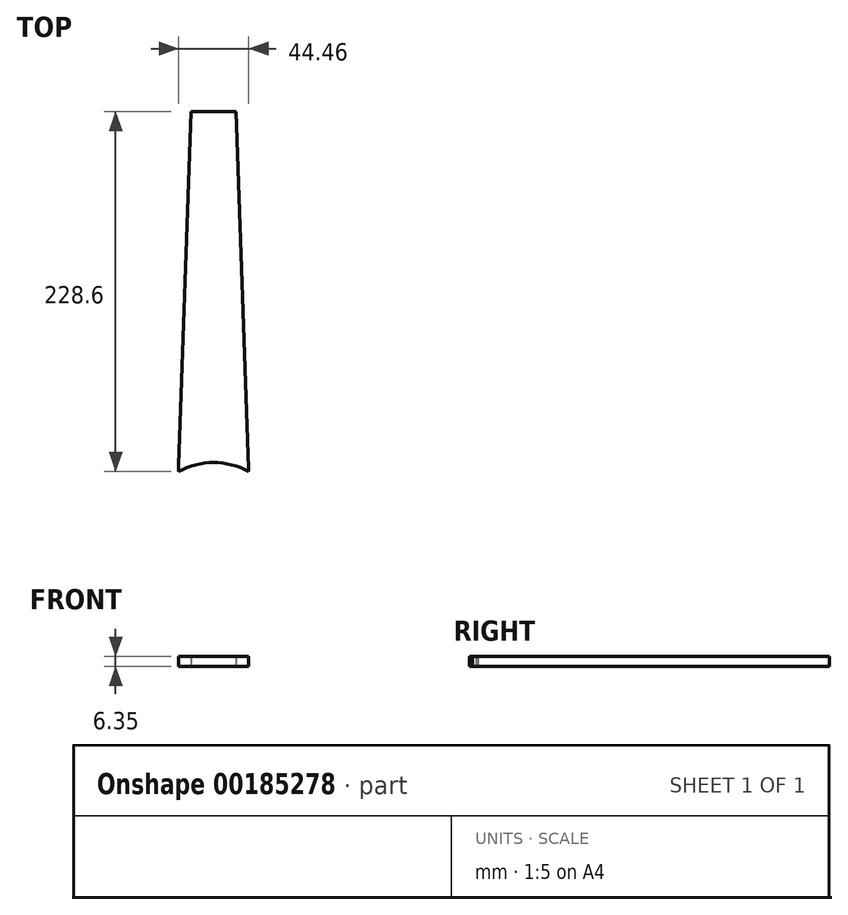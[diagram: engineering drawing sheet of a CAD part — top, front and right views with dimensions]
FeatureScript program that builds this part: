
annotation { "Feature Type Name" : "Feature", "Feature Type Description" : "" }
export const myFeature = defineFeature(function(context is Context, id is Id, definition is map)
    precondition{}
    {
        {
            var Q0;
            Q0=qCreatedBy(makeId("Top.planeOp"),FACE);
            var sketch = newSketch(context, id + "F0", { "sketchPlane" : qUnion([Q0])});
            skLineSegment(sketch, "E0.bottom", {"start": v(-22.22, 0) * mm, "end": v(22.22, 0) * mm});
            skLineSegment(sketch, "E0.top", {"start": v(-22.22, -228.6) * mm, "end": v(22.22, -228.6) * mm});
            skLineSegment(sketch, "E0.left", {"start": v(-22.22, 0) * mm, "end": v(-22.22, -228.6) * mm});
            skLineSegment(sketch, "E0.right", {"start": v(22.23, 0) * mm, "end": v(22.23, -228.6) * mm});
            skSolve(sketch);
        }
        {
            var Q0;
            Q0 = qSketchRegion(id + "F0", true);
            extrude(context, id + "F1", {"entities" : qUnion([Q0]), "oppositeDirection" : true, "depth" : 6.35 * mm});
        }
        {
            var Q0;
            Q0=makeQuery(id+"F1.opExtrude","SWEPT_FACE",FACE,{"disambiguationData":[OSD([sQuery(id+"F0.wireOp",EDGE,"E0.right")])]});
            var sketch = newSketch(context, id + "F2", { "sketchPlane" : qUnion([Q0])});
            skLineSegment(sketch, "E1.0", {"start": v(-21.03, -6.35) * mm, "end": v(-21.03, 0) * mm});
            skLineSegment(sketch, "E2.0", {"start": v(-40.87, -6.35) * mm, "end": v(-40.87, 0) * mm});
            skLineSegment(sketch, "E3.0", {"start": v(-59.61, -6.35) * mm, "end": v(-59.61, 0) * mm});
            skLineSegment(sketch, "E4.0", {"start": v(-77.3, -6.35) * mm, "end": v(-77.3, 0) * mm});
            skLineSegment(sketch, "E5.0", {"start": v(-93.98, -6.35) * mm, "end": v(-93.98, 0) * mm});
            skLineSegment(sketch, "E6.0", {"start": v(-109.73, -6.35) * mm, "end": v(-109.73, 0) * mm});
            skLineSegment(sketch, "E7.0", {"start": v(-124.61, -6.35) * mm, "end": v(-124.61, 0) * mm});
            skLineSegment(sketch, "E8.0", {"start": v(-138.63, -6.35) * mm, "end": v(-138.63, 0) * mm});
            skLineSegment(sketch, "E9.0", {"start": v(-151.9, -6.35) * mm, "end": v(-151.9, 0) * mm});
            skLineSegment(sketch, "E10.0", {"start": v(-164.39, -6.35) * mm, "end": v(-164.39, 0) * mm});
            skLineSegment(sketch, "E11.0", {"start": v(-176.17, -6.35) * mm, "end": v(-176.17, 0) * mm});
            skLineSegment(sketch, "E12.0", {"start": v(-187.33, -6.35) * mm, "end": v(-187.33, 0) * mm});
            skCircle(sketch, "E13", {"center": v(-21.03, 0) * mm, "radius": 0.8 * mm});
            skCircle(sketch, "E14", {"center": v(-40.87, 0) * mm, "radius": 0.8 * mm});
            skCircle(sketch, "E15", {"center": v(-59.61, 0) * mm, "radius": 0.8 * mm});
            skCircle(sketch, "E16", {"center": v(-77.3, 0) * mm, "radius": 0.8 * mm});
            skCircle(sketch, "E17", {"center": v(-93.98, 0) * mm, "radius": 0.8 * mm});
            skCircle(sketch, "E18", {"center": v(-109.73, 0) * mm, "radius": 0.8 * mm});
            skCircle(sketch, "E19", {"center": v(-124.61, 0) * mm, "radius": 0.8 * mm});
            skCircle(sketch, "E20", {"center": v(-138.63, 0) * mm, "radius": 0.8 * mm});
            skCircle(sketch, "E21", {"center": v(-151.9, 0) * mm, "radius": 0.8 * mm});
            skCircle(sketch, "E22", {"center": v(-164.39, 0) * mm, "radius": 0.8 * mm});
            skCircle(sketch, "E23", {"center": v(-176.17, 0) * mm, "radius": 0.8 * mm});
            skCircle(sketch, "E24", {"center": v(-187.33, 0) * mm, "radius": 0.8 * mm});
            skSolve(sketch);
        }
        {
            var Q0;
            {var subQ0=sQuery(id+"F2.wireOp",EDGE,"E1.0");var subQ1=makeQuery(id+"F1.opExtrude","CAP_EDGE",EDGE,{"disambiguationData":[OSD([sQuery(id+"F0.wireOp",EDGE,"E0.right")])],"isStart":true});var subQ2=makeQuery(id+"F2.imprint","INTERSECT",VERTEX,{"derivedFrom":[subQ1,subQ0]});Q0=makeQuery(id+"F2.imprint","IMPRINT",FACE,{"disambiguationData":[TD([[makeQuery(id+"F2.imprint","IMPRINT",EDGE,{"disambiguationData":[TD([[subQ2,1.0]])],"derivedFrom":subQ0}),1.0]])]});}
            var Q1;
            {var subQ0=sQuery(id+"F2.wireOp",EDGE,"E1.0");var subQ1=makeQuery(id+"F1.opExtrude","CAP_EDGE",EDGE,{"disambiguationData":[OSD([sQuery(id+"F0.wireOp",EDGE,"E0.right")])],"isStart":true});var subQ2=makeQuery(id+"F2.imprint","INTERSECT",VERTEX,{"derivedFrom":[subQ1,subQ0]});Q1=makeQuery(id+"F2.imprint","IMPRINT",FACE,{"disambiguationData":[TD([[makeQuery(id+"F2.imprint","IMPRINT",EDGE,{"disambiguationData":[TD([[subQ2,1.0]])],"derivedFrom":subQ0}),-1.0]])]});}
            var Q2;
            {var subQ0=sQuery(id+"F2.wireOp",EDGE,"E2.0");var subQ1=makeQuery(id+"F1.opExtrude","CAP_EDGE",EDGE,{"disambiguationData":[OSD([sQuery(id+"F0.wireOp",EDGE,"E0.right")])],"isStart":true});var subQ2=makeQuery(id+"F2.imprint","INTERSECT",VERTEX,{"derivedFrom":[subQ1,subQ0]});Q2=makeQuery(id+"F2.imprint","IMPRINT",FACE,{"disambiguationData":[TD([[makeQuery(id+"F2.imprint","IMPRINT",EDGE,{"disambiguationData":[TD([[subQ2,1.0]])],"derivedFrom":subQ0}),1.0]])]});}
            var Q3;
            {var subQ0=sQuery(id+"F2.wireOp",EDGE,"E2.0");var subQ1=makeQuery(id+"F1.opExtrude","CAP_EDGE",EDGE,{"disambiguationData":[OSD([sQuery(id+"F0.wireOp",EDGE,"E0.right")])],"isStart":true});var subQ2=makeQuery(id+"F2.imprint","INTERSECT",VERTEX,{"derivedFrom":[subQ1,subQ0]});Q3=makeQuery(id+"F2.imprint","IMPRINT",FACE,{"disambiguationData":[TD([[makeQuery(id+"F2.imprint","IMPRINT",EDGE,{"disambiguationData":[TD([[subQ2,1.0]])],"derivedFrom":subQ0}),-1.0]])]});}
            var Q4;
            {var subQ0=sQuery(id+"F2.wireOp",EDGE,"E3.0");var subQ1=makeQuery(id+"F1.opExtrude","CAP_EDGE",EDGE,{"disambiguationData":[OSD([sQuery(id+"F0.wireOp",EDGE,"E0.right")])],"isStart":true});var subQ2=makeQuery(id+"F2.imprint","INTERSECT",VERTEX,{"derivedFrom":[subQ1,subQ0]});Q4=makeQuery(id+"F2.imprint","IMPRINT",FACE,{"disambiguationData":[TD([[makeQuery(id+"F2.imprint","IMPRINT",EDGE,{"disambiguationData":[TD([[subQ2,1.0]])],"derivedFrom":subQ0}),1.0]])]});}
            var Q5;
            {var subQ0=sQuery(id+"F2.wireOp",EDGE,"E3.0");var subQ1=makeQuery(id+"F1.opExtrude","CAP_EDGE",EDGE,{"disambiguationData":[OSD([sQuery(id+"F0.wireOp",EDGE,"E0.right")])],"isStart":true});var subQ2=makeQuery(id+"F2.imprint","INTERSECT",VERTEX,{"derivedFrom":[subQ1,subQ0]});Q5=makeQuery(id+"F2.imprint","IMPRINT",FACE,{"disambiguationData":[TD([[makeQuery(id+"F2.imprint","IMPRINT",EDGE,{"disambiguationData":[TD([[subQ2,1.0]])],"derivedFrom":subQ0}),-1.0]])]});}
            var Q6;
            {var subQ0=sQuery(id+"F2.wireOp",EDGE,"E4.0");var subQ1=makeQuery(id+"F1.opExtrude","CAP_EDGE",EDGE,{"disambiguationData":[OSD([sQuery(id+"F0.wireOp",EDGE,"E0.right")])],"isStart":true});var subQ2=makeQuery(id+"F2.imprint","INTERSECT",VERTEX,{"derivedFrom":[subQ1,subQ0]});Q6=makeQuery(id+"F2.imprint","IMPRINT",FACE,{"disambiguationData":[TD([[makeQuery(id+"F2.imprint","IMPRINT",EDGE,{"disambiguationData":[TD([[subQ2,1.0]])],"derivedFrom":subQ0}),1.0]])]});}
            var Q7;
            {var subQ0=sQuery(id+"F2.wireOp",EDGE,"E4.0");var subQ1=makeQuery(id+"F1.opExtrude","CAP_EDGE",EDGE,{"disambiguationData":[OSD([sQuery(id+"F0.wireOp",EDGE,"E0.right")])],"isStart":true});var subQ2=makeQuery(id+"F2.imprint","INTERSECT",VERTEX,{"derivedFrom":[subQ1,subQ0]});Q7=makeQuery(id+"F2.imprint","IMPRINT",FACE,{"disambiguationData":[TD([[makeQuery(id+"F2.imprint","IMPRINT",EDGE,{"disambiguationData":[TD([[subQ2,1.0]])],"derivedFrom":subQ0}),-1.0]])]});}
            var Q8;
            {var subQ0=sQuery(id+"F2.wireOp",EDGE,"E5.0");var subQ1=makeQuery(id+"F1.opExtrude","CAP_EDGE",EDGE,{"disambiguationData":[OSD([sQuery(id+"F0.wireOp",EDGE,"E0.right")])],"isStart":true});var subQ2=makeQuery(id+"F2.imprint","INTERSECT",VERTEX,{"derivedFrom":[subQ1,subQ0]});Q8=makeQuery(id+"F2.imprint","IMPRINT",FACE,{"disambiguationData":[TD([[makeQuery(id+"F2.imprint","IMPRINT",EDGE,{"disambiguationData":[TD([[subQ2,1.0]])],"derivedFrom":subQ0}),1.0]])]});}
            var Q9;
            {var subQ0=sQuery(id+"F2.wireOp",EDGE,"E5.0");var subQ1=makeQuery(id+"F1.opExtrude","CAP_EDGE",EDGE,{"disambiguationData":[OSD([sQuery(id+"F0.wireOp",EDGE,"E0.right")])],"isStart":true});var subQ2=makeQuery(id+"F2.imprint","INTERSECT",VERTEX,{"derivedFrom":[subQ1,subQ0]});Q9=makeQuery(id+"F2.imprint","IMPRINT",FACE,{"disambiguationData":[TD([[makeQuery(id+"F2.imprint","IMPRINT",EDGE,{"disambiguationData":[TD([[subQ2,1.0]])],"derivedFrom":subQ0}),-1.0]])]});}
            var Q10;
            {var subQ0=sQuery(id+"F2.wireOp",EDGE,"E6.0");var subQ1=makeQuery(id+"F1.opExtrude","CAP_EDGE",EDGE,{"disambiguationData":[OSD([sQuery(id+"F0.wireOp",EDGE,"E0.right")])],"isStart":true});var subQ2=makeQuery(id+"F2.imprint","INTERSECT",VERTEX,{"derivedFrom":[subQ1,subQ0]});Q10=makeQuery(id+"F2.imprint","IMPRINT",FACE,{"disambiguationData":[TD([[makeQuery(id+"F2.imprint","IMPRINT",EDGE,{"disambiguationData":[TD([[subQ2,1.0]])],"derivedFrom":subQ0}),1.0]])]});}
            var Q11;
            {var subQ0=sQuery(id+"F2.wireOp",EDGE,"E6.0");var subQ1=makeQuery(id+"F1.opExtrude","CAP_EDGE",EDGE,{"disambiguationData":[OSD([sQuery(id+"F0.wireOp",EDGE,"E0.right")])],"isStart":true});var subQ2=makeQuery(id+"F2.imprint","INTERSECT",VERTEX,{"derivedFrom":[subQ1,subQ0]});Q11=makeQuery(id+"F2.imprint","IMPRINT",FACE,{"disambiguationData":[TD([[makeQuery(id+"F2.imprint","IMPRINT",EDGE,{"disambiguationData":[TD([[subQ2,1.0]])],"derivedFrom":subQ0}),-1.0]])]});}
            var Q12;
            {var subQ0=sQuery(id+"F2.wireOp",EDGE,"E7.0");var subQ1=makeQuery(id+"F1.opExtrude","CAP_EDGE",EDGE,{"disambiguationData":[OSD([sQuery(id+"F0.wireOp",EDGE,"E0.right")])],"isStart":true});var subQ2=makeQuery(id+"F2.imprint","INTERSECT",VERTEX,{"derivedFrom":[subQ1,subQ0]});Q12=makeQuery(id+"F2.imprint","IMPRINT",FACE,{"disambiguationData":[TD([[makeQuery(id+"F2.imprint","IMPRINT",EDGE,{"disambiguationData":[TD([[subQ2,1.0]])],"derivedFrom":subQ0}),1.0]])]});}
            var Q13;
            {var subQ0=sQuery(id+"F2.wireOp",EDGE,"E7.0");var subQ1=makeQuery(id+"F1.opExtrude","CAP_EDGE",EDGE,{"disambiguationData":[OSD([sQuery(id+"F0.wireOp",EDGE,"E0.right")])],"isStart":true});var subQ2=makeQuery(id+"F2.imprint","INTERSECT",VERTEX,{"derivedFrom":[subQ1,subQ0]});Q13=makeQuery(id+"F2.imprint","IMPRINT",FACE,{"disambiguationData":[TD([[makeQuery(id+"F2.imprint","IMPRINT",EDGE,{"disambiguationData":[TD([[subQ2,1.0]])],"derivedFrom":subQ0}),-1.0]])]});}
            var Q14;
            {var subQ0=sQuery(id+"F2.wireOp",EDGE,"E8.0");var subQ1=makeQuery(id+"F1.opExtrude","CAP_EDGE",EDGE,{"disambiguationData":[OSD([sQuery(id+"F0.wireOp",EDGE,"E0.right")])],"isStart":true});var subQ2=makeQuery(id+"F2.imprint","INTERSECT",VERTEX,{"derivedFrom":[subQ1,subQ0]});Q14=makeQuery(id+"F2.imprint","IMPRINT",FACE,{"disambiguationData":[TD([[makeQuery(id+"F2.imprint","IMPRINT",EDGE,{"disambiguationData":[TD([[subQ2,1.0]])],"derivedFrom":subQ0}),1.0]])]});}
            var Q15;
            {var subQ0=sQuery(id+"F2.wireOp",EDGE,"E8.0");var subQ1=makeQuery(id+"F1.opExtrude","CAP_EDGE",EDGE,{"disambiguationData":[OSD([sQuery(id+"F0.wireOp",EDGE,"E0.right")])],"isStart":true});var subQ2=makeQuery(id+"F2.imprint","INTERSECT",VERTEX,{"derivedFrom":[subQ1,subQ0]});Q15=makeQuery(id+"F2.imprint","IMPRINT",FACE,{"disambiguationData":[TD([[makeQuery(id+"F2.imprint","IMPRINT",EDGE,{"disambiguationData":[TD([[subQ2,1.0]])],"derivedFrom":subQ0}),-1.0]])]});}
            var Q16;
            {var subQ0=sQuery(id+"F2.wireOp",EDGE,"E9.0");var subQ1=makeQuery(id+"F1.opExtrude","CAP_EDGE",EDGE,{"disambiguationData":[OSD([sQuery(id+"F0.wireOp",EDGE,"E0.right")])],"isStart":true});var subQ2=makeQuery(id+"F2.imprint","INTERSECT",VERTEX,{"derivedFrom":[subQ1,subQ0]});Q16=makeQuery(id+"F2.imprint","IMPRINT",FACE,{"disambiguationData":[TD([[makeQuery(id+"F2.imprint","IMPRINT",EDGE,{"disambiguationData":[TD([[subQ2,1.0]])],"derivedFrom":subQ0}),1.0]])]});}
            var Q17;
            {var subQ0=sQuery(id+"F2.wireOp",EDGE,"E9.0");var subQ1=makeQuery(id+"F1.opExtrude","CAP_EDGE",EDGE,{"disambiguationData":[OSD([sQuery(id+"F0.wireOp",EDGE,"E0.right")])],"isStart":true});var subQ2=makeQuery(id+"F2.imprint","INTERSECT",VERTEX,{"derivedFrom":[subQ1,subQ0]});Q17=makeQuery(id+"F2.imprint","IMPRINT",FACE,{"disambiguationData":[TD([[makeQuery(id+"F2.imprint","IMPRINT",EDGE,{"disambiguationData":[TD([[subQ2,1.0]])],"derivedFrom":subQ0}),-1.0]])]});}
            var Q18;
            {var subQ0=sQuery(id+"F2.wireOp",EDGE,"E10.0");var subQ1=makeQuery(id+"F1.opExtrude","CAP_EDGE",EDGE,{"disambiguationData":[OSD([sQuery(id+"F0.wireOp",EDGE,"E0.right")])],"isStart":true});var subQ2=makeQuery(id+"F2.imprint","INTERSECT",VERTEX,{"derivedFrom":[subQ1,subQ0]});Q18=makeQuery(id+"F2.imprint","IMPRINT",FACE,{"disambiguationData":[TD([[makeQuery(id+"F2.imprint","IMPRINT",EDGE,{"disambiguationData":[TD([[subQ2,1.0]])],"derivedFrom":subQ0}),1.0]])]});}
            var Q19;
            {var subQ0=sQuery(id+"F2.wireOp",EDGE,"E10.0");var subQ1=makeQuery(id+"F1.opExtrude","CAP_EDGE",EDGE,{"disambiguationData":[OSD([sQuery(id+"F0.wireOp",EDGE,"E0.right")])],"isStart":true});var subQ2=makeQuery(id+"F2.imprint","INTERSECT",VERTEX,{"derivedFrom":[subQ1,subQ0]});Q19=makeQuery(id+"F2.imprint","IMPRINT",FACE,{"disambiguationData":[TD([[makeQuery(id+"F2.imprint","IMPRINT",EDGE,{"disambiguationData":[TD([[subQ2,1.0]])],"derivedFrom":subQ0}),-1.0]])]});}
            var Q20;
            {var subQ0=sQuery(id+"F2.wireOp",EDGE,"E11.0");var subQ1=makeQuery(id+"F1.opExtrude","CAP_EDGE",EDGE,{"disambiguationData":[OSD([sQuery(id+"F0.wireOp",EDGE,"E0.right")])],"isStart":true});var subQ2=makeQuery(id+"F2.imprint","INTERSECT",VERTEX,{"derivedFrom":[subQ1,subQ0]});Q20=makeQuery(id+"F2.imprint","IMPRINT",FACE,{"disambiguationData":[TD([[makeQuery(id+"F2.imprint","IMPRINT",EDGE,{"disambiguationData":[TD([[subQ2,1.0]])],"derivedFrom":subQ0}),1.0]])]});}
            var Q21;
            {var subQ0=sQuery(id+"F2.wireOp",EDGE,"E11.0");var subQ1=makeQuery(id+"F1.opExtrude","CAP_EDGE",EDGE,{"disambiguationData":[OSD([sQuery(id+"F0.wireOp",EDGE,"E0.right")])],"isStart":true});var subQ2=makeQuery(id+"F2.imprint","INTERSECT",VERTEX,{"derivedFrom":[subQ1,subQ0]});Q21=makeQuery(id+"F2.imprint","IMPRINT",FACE,{"disambiguationData":[TD([[makeQuery(id+"F2.imprint","IMPRINT",EDGE,{"disambiguationData":[TD([[subQ2,1.0]])],"derivedFrom":subQ0}),-1.0]])]});}
            var Q22;
            {var subQ0=sQuery(id+"F2.wireOp",EDGE,"E12.0");var subQ1=makeQuery(id+"F1.opExtrude","CAP_EDGE",EDGE,{"disambiguationData":[OSD([sQuery(id+"F0.wireOp",EDGE,"E0.right")])],"isStart":true});var subQ2=makeQuery(id+"F2.imprint","INTERSECT",VERTEX,{"derivedFrom":[subQ1,subQ0]});Q22=makeQuery(id+"F2.imprint","IMPRINT",FACE,{"disambiguationData":[TD([[makeQuery(id+"F2.imprint","IMPRINT",EDGE,{"disambiguationData":[TD([[subQ2,1.0]])],"derivedFrom":subQ0}),1.0]])]});}
            var Q23;
            {var subQ0=sQuery(id+"F2.wireOp",EDGE,"E12.0");var subQ1=makeQuery(id+"F1.opExtrude","CAP_EDGE",EDGE,{"disambiguationData":[OSD([sQuery(id+"F0.wireOp",EDGE,"E0.right")])],"isStart":true});var subQ2=makeQuery(id+"F2.imprint","INTERSECT",VERTEX,{"derivedFrom":[subQ1,subQ0]});Q23=makeQuery(id+"F2.imprint","IMPRINT",FACE,{"disambiguationData":[TD([[makeQuery(id+"F2.imprint","IMPRINT",EDGE,{"disambiguationData":[TD([[subQ2,1.0]])],"derivedFrom":subQ0}),-1.0]])]});}
            var Q24;
            {var subQ0=sQuery(id+"F2.wireOp",EDGE,"E14");var subQ1=makeQuery(id+"F1.opExtrude","CAP_EDGE",EDGE,{"disambiguationData":[OSD([sQuery(id+"F0.wireOp",EDGE,"E0.right")])],"isStart":true});var subQ2=makeQuery(id+"F2.imprint","INTERSECT",VERTEX,{"disambiguationData":[OD(0.0)],"derivedFrom":[subQ1,subQ0]});Q24=makeQuery(id+"F2.imprint","IMPRINT",FACE,{"disambiguationData":[TD([[makeQuery(id+"F2.imprint","IMPRINT",EDGE,{"disambiguationData":[TD([[subQ2,1.0]])],"derivedFrom":subQ0}),1.0]])]});}
            var Q25;
            {var subQ0=sQuery(id+"F2.wireOp",EDGE,"E15");var subQ1=makeQuery(id+"F1.opExtrude","CAP_EDGE",EDGE,{"disambiguationData":[OSD([sQuery(id+"F0.wireOp",EDGE,"E0.right")])],"isStart":true});var subQ2=makeQuery(id+"F2.imprint","INTERSECT",VERTEX,{"disambiguationData":[OD(0.0)],"derivedFrom":[subQ1,subQ0]});Q25=makeQuery(id+"F2.imprint","IMPRINT",FACE,{"disambiguationData":[TD([[makeQuery(id+"F2.imprint","IMPRINT",EDGE,{"disambiguationData":[TD([[subQ2,1.0]])],"derivedFrom":subQ0}),1.0]])]});}
            var Q26;
            {var subQ0=sQuery(id+"F2.wireOp",EDGE,"E16");var subQ1=makeQuery(id+"F1.opExtrude","CAP_EDGE",EDGE,{"disambiguationData":[OSD([sQuery(id+"F0.wireOp",EDGE,"E0.right")])],"isStart":true});var subQ2=makeQuery(id+"F2.imprint","INTERSECT",VERTEX,{"disambiguationData":[OD(0.0)],"derivedFrom":[subQ1,subQ0]});Q26=makeQuery(id+"F2.imprint","IMPRINT",FACE,{"disambiguationData":[TD([[makeQuery(id+"F2.imprint","IMPRINT",EDGE,{"disambiguationData":[TD([[subQ2,1.0]])],"derivedFrom":subQ0}),1.0]])]});}
            var Q27;
            {var subQ0=sQuery(id+"F2.wireOp",EDGE,"E17");var subQ1=makeQuery(id+"F1.opExtrude","CAP_EDGE",EDGE,{"disambiguationData":[OSD([sQuery(id+"F0.wireOp",EDGE,"E0.right")])],"isStart":true});var subQ2=makeQuery(id+"F2.imprint","INTERSECT",VERTEX,{"disambiguationData":[OD(0.0)],"derivedFrom":[subQ1,subQ0]});Q27=makeQuery(id+"F2.imprint","IMPRINT",FACE,{"disambiguationData":[TD([[makeQuery(id+"F2.imprint","IMPRINT",EDGE,{"disambiguationData":[TD([[subQ2,1.0]])],"derivedFrom":subQ0}),1.0]])]});}
            var Q28;
            {var subQ0=sQuery(id+"F2.wireOp",EDGE,"E18");var subQ1=makeQuery(id+"F1.opExtrude","CAP_EDGE",EDGE,{"disambiguationData":[OSD([sQuery(id+"F0.wireOp",EDGE,"E0.right")])],"isStart":true});var subQ2=makeQuery(id+"F2.imprint","INTERSECT",VERTEX,{"disambiguationData":[OD(0.0)],"derivedFrom":[subQ1,subQ0]});Q28=makeQuery(id+"F2.imprint","IMPRINT",FACE,{"disambiguationData":[TD([[makeQuery(id+"F2.imprint","IMPRINT",EDGE,{"disambiguationData":[TD([[subQ2,1.0]])],"derivedFrom":subQ0}),1.0]])]});}
            var Q29;
            {var subQ0=sQuery(id+"F2.wireOp",EDGE,"E19");var subQ1=makeQuery(id+"F1.opExtrude","CAP_EDGE",EDGE,{"disambiguationData":[OSD([sQuery(id+"F0.wireOp",EDGE,"E0.right")])],"isStart":true});var subQ2=makeQuery(id+"F2.imprint","INTERSECT",VERTEX,{"disambiguationData":[OD(0.0)],"derivedFrom":[subQ1,subQ0]});Q29=makeQuery(id+"F2.imprint","IMPRINT",FACE,{"disambiguationData":[TD([[makeQuery(id+"F2.imprint","IMPRINT",EDGE,{"disambiguationData":[TD([[subQ2,1.0]])],"derivedFrom":subQ0}),1.0]])]});}
            var Q30;
            {var subQ0=sQuery(id+"F2.wireOp",EDGE,"E20");var subQ1=makeQuery(id+"F1.opExtrude","CAP_EDGE",EDGE,{"disambiguationData":[OSD([sQuery(id+"F0.wireOp",EDGE,"E0.right")])],"isStart":true});var subQ2=makeQuery(id+"F2.imprint","INTERSECT",VERTEX,{"disambiguationData":[OD(0.0)],"derivedFrom":[subQ1,subQ0]});Q30=makeQuery(id+"F2.imprint","IMPRINT",FACE,{"disambiguationData":[TD([[makeQuery(id+"F2.imprint","IMPRINT",EDGE,{"disambiguationData":[TD([[subQ2,1.0]])],"derivedFrom":subQ0}),1.0]])]});}
            var Q31;
            {var subQ0=sQuery(id+"F2.wireOp",EDGE,"E21");var subQ1=makeQuery(id+"F1.opExtrude","CAP_EDGE",EDGE,{"disambiguationData":[OSD([sQuery(id+"F0.wireOp",EDGE,"E0.right")])],"isStart":true});var subQ2=makeQuery(id+"F2.imprint","INTERSECT",VERTEX,{"disambiguationData":[OD(0.0)],"derivedFrom":[subQ1,subQ0]});Q31=makeQuery(id+"F2.imprint","IMPRINT",FACE,{"disambiguationData":[TD([[makeQuery(id+"F2.imprint","IMPRINT",EDGE,{"disambiguationData":[TD([[subQ2,1.0]])],"derivedFrom":subQ0}),1.0]])]});}
            var Q32;
            {var subQ0=sQuery(id+"F2.wireOp",EDGE,"E22");var subQ1=makeQuery(id+"F1.opExtrude","CAP_EDGE",EDGE,{"disambiguationData":[OSD([sQuery(id+"F0.wireOp",EDGE,"E0.right")])],"isStart":true});var subQ2=makeQuery(id+"F2.imprint","INTERSECT",VERTEX,{"disambiguationData":[OD(0.0)],"derivedFrom":[subQ1,subQ0]});Q32=makeQuery(id+"F2.imprint","IMPRINT",FACE,{"disambiguationData":[TD([[makeQuery(id+"F2.imprint","IMPRINT",EDGE,{"disambiguationData":[TD([[subQ2,1.0]])],"derivedFrom":subQ0}),1.0]])]});}
            var Q33;
            {var subQ0=sQuery(id+"F2.wireOp",EDGE,"E23");var subQ1=makeQuery(id+"F1.opExtrude","CAP_EDGE",EDGE,{"disambiguationData":[OSD([sQuery(id+"F0.wireOp",EDGE,"E0.right")])],"isStart":true});var subQ2=makeQuery(id+"F2.imprint","INTERSECT",VERTEX,{"disambiguationData":[OD(0.0)],"derivedFrom":[subQ1,subQ0]});Q33=makeQuery(id+"F2.imprint","IMPRINT",FACE,{"disambiguationData":[TD([[makeQuery(id+"F2.imprint","IMPRINT",EDGE,{"disambiguationData":[TD([[subQ2,1.0]])],"derivedFrom":subQ0}),1.0]])]});}
            var Q34;
            {var subQ0=sQuery(id+"F2.wireOp",EDGE,"E24");var subQ1=makeQuery(id+"F1.opExtrude","CAP_EDGE",EDGE,{"disambiguationData":[OSD([sQuery(id+"F0.wireOp",EDGE,"E0.right")])],"isStart":true});var subQ2=makeQuery(id+"F2.imprint","INTERSECT",VERTEX,{"disambiguationData":[OD(0.0)],"derivedFrom":[subQ1,subQ0]});Q34=makeQuery(id+"F2.imprint","IMPRINT",FACE,{"disambiguationData":[TD([[makeQuery(id+"F2.imprint","IMPRINT",EDGE,{"disambiguationData":[TD([[subQ2,1.0]])],"derivedFrom":subQ0}),1.0]])]});}
            var Q35;
            {var subQ0=sQuery(id+"F2.wireOp",EDGE,"E13");var subQ1=makeQuery(id+"F1.opExtrude","CAP_EDGE",EDGE,{"disambiguationData":[OSD([sQuery(id+"F0.wireOp",EDGE,"E0.right")])],"isStart":true});var subQ2=makeQuery(id+"F2.imprint","INTERSECT",VERTEX,{"disambiguationData":[OD(0.0)],"derivedFrom":[subQ1,subQ0]});Q35=makeQuery(id+"F2.imprint","IMPRINT",FACE,{"disambiguationData":[TD([[makeQuery(id+"F2.imprint","IMPRINT",EDGE,{"disambiguationData":[TD([[subQ2,1.0]])],"derivedFrom":subQ0}),1.0]])]});}
            extrude(context, id + "F3", {"entities" : qUnion([Q0, Q1, Q2, Q3, Q4, Q5, Q6, Q7, Q8, Q9, Q10, Q11, Q12, Q13, Q14, Q15, Q16, Q17, Q18, Q19, Q20, Q21, Q22, Q23, Q24, Q25, Q26, Q27, Q28, Q29, Q30, Q31, Q32, Q33, Q34, Q35]), "operationType" : NewBodyOperationType.ADD, "oppositeDirection" : true, "depth" : 44.45 * mm});
        }
        {
            var Q0;
            Q0=qCreatedBy(makeId("Top.planeOp"),FACE);
            var sketch = newSketch(context, id + "F4", { "sketchPlane" : qUnion([Q0])});
            skLineSegment(sketch, "E25.0", {"start": v(14.29, 0) * mm, "end": v(14.29, -20.24) * mm});
            skLineSegment(sketch, "E26.0", {"start": v(-14.29, 0) * mm, "end": v(-14.29, -20.24) * mm});
            skLineSegment(sketch, "E27", {"start": v(-22.36, 0) * mm, "end": v(22.29, 0) * mm});
            skLineSegment(sketch, "E28.0", {"start": v(-22.36, -228.6) * mm, "end": v(22.29, -228.6) * mm});
            skLineSegment(sketch, "E29", {"start": v(-22.36, -228.6) * mm, "end": v(-14.29, 0) * mm});
            skLineSegment(sketch, "E30", {"start": v(14.29, 0) * mm, "end": v(22.29, -228.6) * mm});
            skLineSegment(sketch, "E31", {"start": v(22.29, 0) * mm, "end": v(22.29, -228.6) * mm});
            skLineSegment(sketch, "E32", {"start": v(-22.36, 0) * mm, "end": v(-22.36, -228.6) * mm});
            skSolve(sketch);
        }
        {
            var Q0;
            {var subQ0=sQuery(id+"F4.wireOp",EDGE,"E30");Q0=makeQuery(id+"F4.imprint","IMPRINT",FACE,{"disambiguationData":[TD([[makeQuery(id+"F4.imprint","IMPRINT",EDGE,{"derivedFrom":subQ0}),1.0]])]});}
            var Q1;
            {var subQ0=sQuery(id+"F4.wireOp",EDGE,"E29");Q1=makeQuery(id+"F4.imprint","IMPRINT",FACE,{"disambiguationData":[TD([[makeQuery(id+"F4.imprint","IMPRINT",EDGE,{"derivedFrom":subQ0}),1.0]])]});}
            extrude(context, id + "F5", {"entities" : qUnion([Q0, Q1]), "operationType" : NewBodyOperationType.REMOVE, "endBound" : BoundingType.SYMMETRIC, "depth" : 25.4 * mm});
        }
        {
            var Q0;
            {var subQ0=sQuery(id+"F2.wireOp",EDGE,"E21");var subQ1=sQuery(id+"F2.wireOp",EDGE,"E20");var subQ2=sQuery(id+"F2.wireOp",EDGE,"E19");var subQ3=sQuery(id+"F2.wireOp",EDGE,"E18");var subQ4=sQuery(id+"F2.wireOp",EDGE,"E24");var subQ5=sQuery(id+"F2.wireOp",EDGE,"E17");var subQ6=sQuery(id+"F2.wireOp",EDGE,"E16");var subQ7=sQuery(id+"F2.wireOp",EDGE,"E15");var subQ8=sQuery(id+"F2.wireOp",EDGE,"E13");var subQ9=sQuery(id+"F2.wireOp",EDGE,"E22");var subQ10=sQuery(id+"F0.wireOp",EDGE,"E0.right");var subQ11=sQuery(id+"F0.wireOp",EDGE,"E0.top");var subQ12=sQuery(id+"F0.wireOp",EDGE,"E0.left");var subQ13=sQuery(id+"F2.wireOp",EDGE,"E14");var subQ14=sQuery(id+"F2.wireOp",EDGE,"E23");Q0=makeQuery(id+"F3.boolean.opBoolean","SPLIT",FACE,{"disambiguationData":[TD([makeQuery(id+"F1.opExtrude","SWEPT_FACE",FACE,{"disambiguationData":[OSD([subQ11])]}),makeQuery(id+"F1.opExtrude","SWEPT_FACE",FACE,{"disambiguationData":[OSD([subQ12])]}),makeQuery(id+"F1.opExtrude","SWEPT_FACE",FACE,{"disambiguationData":[OSD([subQ10])]}),makeQuery(id+"F3.opExtrude","CAP_FACE",FACE,{"disambiguationData":[OSD([subQ8])],"isStart":true}),makeQuery(id+"F3.opExtrude","CAP_FACE",FACE,{"disambiguationData":[OSD([subQ8])],"isStart":false}),makeQuery(id+"F3.opExtrude","CAP_FACE",FACE,{"disambiguationData":[OSD([subQ13])],"isStart":true}),makeQuery(id+"F3.opExtrude","CAP_FACE",FACE,{"disambiguationData":[OSD([subQ13])],"isStart":false}),makeQuery(id+"F3.opExtrude","CAP_FACE",FACE,{"disambiguationData":[OSD([subQ7])],"isStart":true}),makeQuery(id+"F3.opExtrude","CAP_FACE",FACE,{"disambiguationData":[OSD([subQ7])],"isStart":false}),makeQuery(id+"F3.opExtrude","CAP_FACE",FACE,{"disambiguationData":[OSD([subQ6])],"isStart":true}),makeQuery(id+"F3.opExtrude","CAP_FACE",FACE,{"disambiguationData":[OSD([subQ6])],"isStart":false}),makeQuery(id+"F3.opExtrude","CAP_FACE",FACE,{"disambiguationData":[OSD([subQ5])],"isStart":true}),makeQuery(id+"F3.opExtrude","CAP_FACE",FACE,{"disambiguationData":[OSD([subQ5])],"isStart":false}),makeQuery(id+"F3.opExtrude","CAP_FACE",FACE,{"disambiguationData":[OSD([subQ3])],"isStart":true}),makeQuery(id+"F3.opExtrude","CAP_FACE",FACE,{"disambiguationData":[OSD([subQ3])],"isStart":false}),makeQuery(id+"F3.opExtrude","CAP_FACE",FACE,{"disambiguationData":[OSD([subQ2])],"isStart":true}),makeQuery(id+"F3.opExtrude","CAP_FACE",FACE,{"disambiguationData":[OSD([subQ2])],"isStart":false}),makeQuery(id+"F3.opExtrude","CAP_FACE",FACE,{"disambiguationData":[OSD([subQ1])],"isStart":true}),makeQuery(id+"F3.opExtrude","CAP_FACE",FACE,{"disambiguationData":[OSD([subQ1])],"isStart":false}),makeQuery(id+"F3.opExtrude","CAP_FACE",FACE,{"disambiguationData":[OSD([subQ0])],"isStart":true}),makeQuery(id+"F3.opExtrude","CAP_FACE",FACE,{"disambiguationData":[OSD([subQ0])],"isStart":false}),makeQuery(id+"F3.opExtrude","CAP_FACE",FACE,{"disambiguationData":[OSD([subQ9])],"isStart":true}),makeQuery(id+"F3.opExtrude","CAP_FACE",FACE,{"disambiguationData":[OSD([subQ9])],"isStart":false}),makeQuery(id+"F3.opExtrude","CAP_FACE",FACE,{"disambiguationData":[OSD([subQ14])],"isStart":true}),makeQuery(id+"F3.opExtrude","CAP_FACE",FACE,{"disambiguationData":[OSD([subQ14])],"isStart":false}),makeQuery(id+"F3.opExtrude","SWEPT_FACE",FACE,{"disambiguationData":[OSD([subQ4])]}),makeQuery(id+"F3.opExtrude","CAP_FACE",FACE,{"disambiguationData":[OSD([subQ4])],"isStart":true}),makeQuery(id+"F3.opExtrude","CAP_FACE",FACE,{"disambiguationData":[OSD([subQ4])],"isStart":false})])],"derivedFrom":makeQuery(id+"F1.opExtrude","CAP_FACE",FACE,{"disambiguationData":[OSD([sQuery(id+"F0.wireOp",EDGE,"E0.bottom"),subQ11,subQ12,subQ10])],"isStart":true})});}
            var sketch = newSketch(context, id + "F6", { "sketchPlane" : qUnion([Q0])});
            skArc(sketch, "E33", {"start": v(22.23, -228.6) * mm, "mid": v(0, -223) * mm, "end": v(-22.22, -228.6) * mm});
            skLineSegment(sketch, "E34", {"start": v(-22.22, -228.6) * mm, "end": v(22.23, -228.6) * mm});
            skSolve(sketch);
        }
        {
            var Q0;
            Q0 = qSketchRegion(id + "F6", true);
            extrude(context, id + "F7", {"entities" : qUnion([Q0]), "operationType" : NewBodyOperationType.REMOVE, "oppositeDirection" : true, "depth" : 25.4 * mm});
        }
    });
